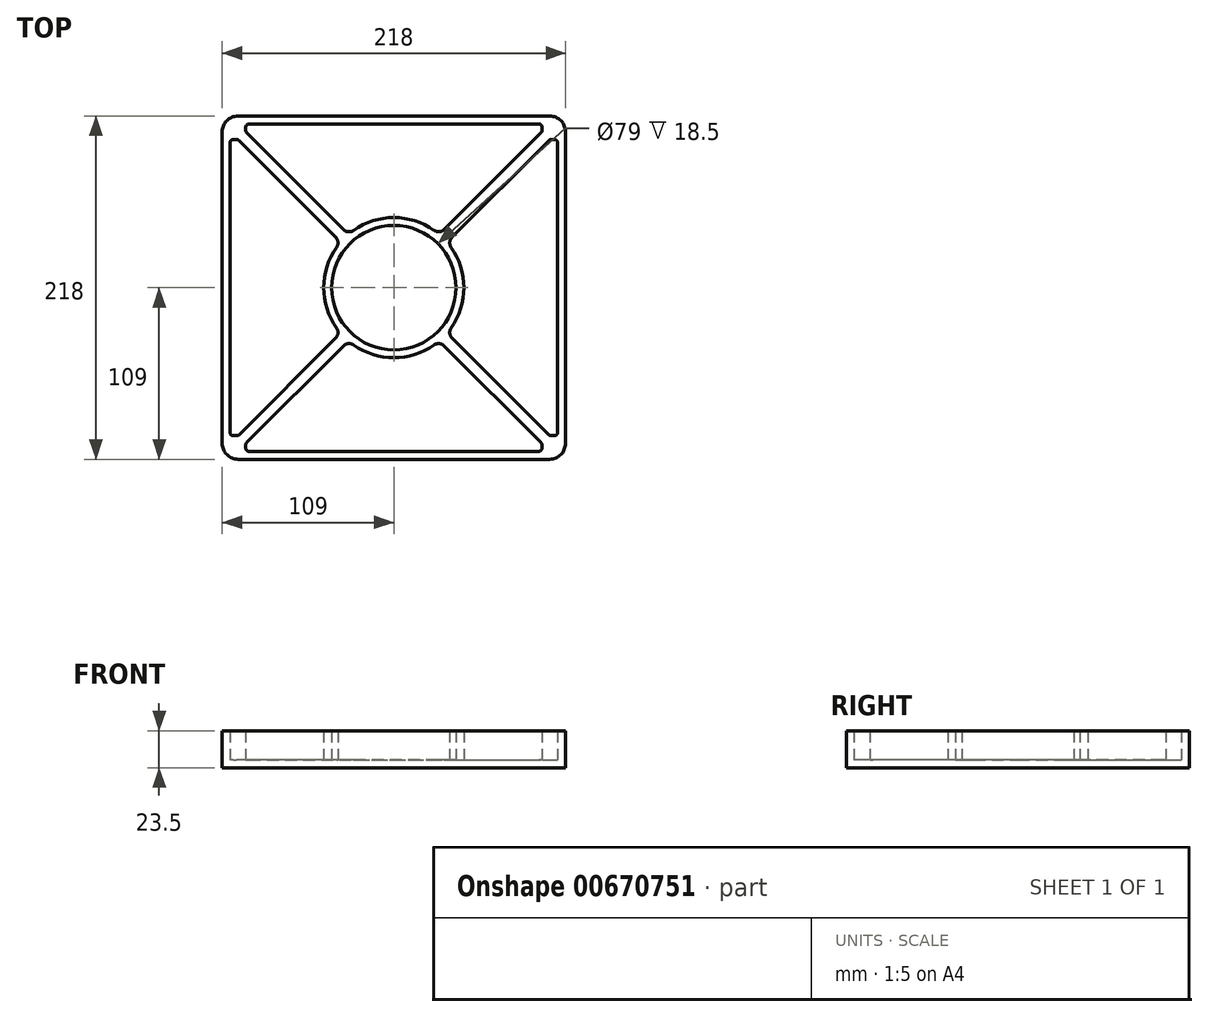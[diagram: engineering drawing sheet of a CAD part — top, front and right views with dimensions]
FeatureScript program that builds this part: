
annotation { "Feature Type Name" : "Feature", "Feature Type Description" : "" }
export const myFeature = defineFeature(function(context is Context, id is Id, definition is map)
    precondition{}
    {
        {
            var Q0;
            Q0=qCreatedBy(makeId("Top.planeOp"),FACE);
            var sketch = newSketch(context, id + "F0", { "sketchPlane" : qUnion([Q0])});
            skLineSegment(sketch, "E0.bottom", {"start": v(-99, 109) * mm, "end": v(99, 109) * mm});
            skLineSegment(sketch, "E0.top", {"start": v(-99, -109) * mm, "end": v(99, -109) * mm});
            skLineSegment(sketch, "E0.left", {"start": v(-109, 99) * mm, "end": v(-109, -99) * mm});
            skLineSegment(sketch, "E0.right", {"start": v(109, 99) * mm, "end": v(109, -99) * mm});
            skLineSegment(sketch, "E1", {"start": v(-109, 109) * mm, "end": v(109, -109) * mm, "construction": true});
            skLineSegment(sketch, "E2", {"start": v(-109, -109) * mm, "end": v(109, 109) * mm, "construction": true});
            skCircle(sketch, "E3", {"center": v(0, 0) * mm, "radius": 39.5 * mm});
            skPoint(sketch, "E4.visualSharp", {"position": v(-109, 109) * mm});
            skArc(sketch, "E4.filletArc", {"start": v(-99, 109) * mm, "mid": v(-106.07, 106.07) * mm, "end": v(-109, 99) * mm});
            skPoint(sketch, "E5.visualSharp", {"position": v(109, 109) * mm});
            skArc(sketch, "E5.filletArc", {"start": v(109, 99) * mm, "mid": v(106.07, 106.07) * mm, "end": v(99, 109) * mm});
            skPoint(sketch, "E6.visualSharp", {"position": v(109, -109) * mm});
            skArc(sketch, "E6.filletArc", {"start": v(99, -109) * mm, "mid": v(106.07, -106.07) * mm, "end": v(109, -99) * mm});
            skPoint(sketch, "E7.visualSharp", {"position": v(-109, -109) * mm});
            skArc(sketch, "E7.filletArc", {"start": v(-109, -99) * mm, "mid": v(-106.07, -106.07) * mm, "end": v(-99, -109) * mm});
            skArc(sketch, "E8.0", {"start": v(-99, 104) * mm, "mid": v(-99.03, 104) * mm, "end": v(-99.05, 104) * mm});
            skLineSegment(sketch, "E8.1", {"start": v(-92.05, 104) * mm, "end": v(-60.86, 104) * mm});
            skLineSegment(sketch, "E8.2", {"start": v(-104, 92.05) * mm, "end": v(-104, 60.86) * mm});
            skArc(sketch, "E8.3", {"start": v(104, 99) * mm, "mid": v(104, 99.03) * mm, "end": v(104, 99.05) * mm});
            skArc(sketch, "E8.4", {"start": v(-104, -99) * mm, "mid": v(-104, -99.03) * mm, "end": v(-104, -99.05) * mm});
            skLineSegment(sketch, "E8.5", {"start": v(-92.05, -104) * mm, "end": v(-60.86, -104) * mm});
            skArc(sketch, "E8.6", {"start": v(99, -104) * mm, "mid": v(99.03, -104) * mm, "end": v(99.05, -104) * mm});
            skLineSegment(sketch, "E8.7", {"start": v(104, 92.05) * mm, "end": v(104, 60.86) * mm});
            skPoint(sketch, "E9.visualSharp", {"position": v(-55.86, 55.86) * mm});
            skPoint(sketch, "E10.visualSharp", {"position": v(55.86, 55.86) * mm});
            skPoint(sketch, "E11.visualSharp", {"position": v(55.86, -55.86) * mm});
            skPoint(sketch, "E12.visualSharp", {"position": v(-55.86, -55.86) * mm});
            skLineSegment(sketch, "E13.trimOffspring", {"start": v(-104, 45.86) * mm, "end": v(-104, -45.86) * mm});
            skLineSegment(sketch, "E14.trimOffspring", {"start": v(-45.86, 104) * mm, "end": v(45.86, 104) * mm});
            skLineSegment(sketch, "E15.trimOffspring", {"start": v(60.86, 104) * mm, "end": v(92.05, 104) * mm});
            skLineSegment(sketch, "E16.trimOffspring", {"start": v(104, 45.86) * mm, "end": v(104, -45.86) * mm});
            skLineSegment(sketch, "E17.trimOffspring", {"start": v(104, -60.86) * mm, "end": v(104, -92.05) * mm});
            skLineSegment(sketch, "E18.trimOffspring", {"start": v(60.86, -104) * mm, "end": v(92.05, -104) * mm});
            skLineSegment(sketch, "E19.trimOffspring", {"start": v(-45.86, -104) * mm, "end": v(45.86, -104) * mm});
            skLineSegment(sketch, "E20.trimOffspring", {"start": v(-104, -60.86) * mm, "end": v(-104, -92.05) * mm});
            skPoint(sketch, "E21.visualSharp", {"position": v(-55.86, 104) * mm});
            skPoint(sketch, "E22.visualSharp", {"position": v(-50.86, 104) * mm});
            skPoint(sketch, "E23.visualSharp", {"position": v(-50.86, 60.45) * mm});
            skPoint(sketch, "E24.visualSharp", {"position": v(-60.45, 50.86) * mm});
            skPoint(sketch, "E25.visualSharp", {"position": v(-104, 50.86) * mm});
            skPoint(sketch, "E26.visualSharp", {"position": v(-104, 55.86) * mm});
            skPoint(sketch, "E27.visualSharp", {"position": v(55.86, 104) * mm});
            skPoint(sketch, "E28.visualSharp", {"position": v(50.86, 104) * mm});
            skPoint(sketch, "E29.visualSharp", {"position": v(50.86, 60.45) * mm});
            skPoint(sketch, "E30.visualSharp", {"position": v(60.45, 50.86) * mm});
            skPoint(sketch, "E31.visualSharp", {"position": v(104, 55.86) * mm});
            skPoint(sketch, "E32.visualSharp", {"position": v(104, 50.86) * mm});
            skPoint(sketch, "E33.visualSharp", {"position": v(104, -50.86) * mm});
            skPoint(sketch, "E34.visualSharp", {"position": v(104, -55.86) * mm});
            skPoint(sketch, "E35.visualSharp", {"position": v(60.45, -50.86) * mm});
            skPoint(sketch, "E36.visualSharp", {"position": v(50.86, -60.45) * mm});
            skPoint(sketch, "E37.visualSharp", {"position": v(55.86, -104) * mm});
            skPoint(sketch, "E38.visualSharp", {"position": v(50.86, -104) * mm});
            skPoint(sketch, "E39.visualSharp", {"position": v(-55.86, -104) * mm});
            skPoint(sketch, "E40.visualSharp", {"position": v(-50.86, -104) * mm});
            skPoint(sketch, "E41.visualSharp", {"position": v(-50.86, -60.45) * mm});
            skPoint(sketch, "E42.visualSharp", {"position": v(-60.45, -50.86) * mm});
            skPoint(sketch, "E43.visualSharp", {"position": v(-104, -50.86) * mm});
            skPoint(sketch, "E44.visualSharp", {"position": v(-104, -55.86) * mm});
            skLineSegment(sketch, "E45", {"start": v(-60.86, 104) * mm, "end": v(-45.86, 104) * mm});
            skLineSegment(sketch, "E46", {"start": v(45.86, 104) * mm, "end": v(60.86, 104) * mm});
            skLineSegment(sketch, "E47", {"start": v(104, 60.86) * mm, "end": v(104, 45.86) * mm});
            skLineSegment(sketch, "E48", {"start": v(104, -45.86) * mm, "end": v(104, -60.86) * mm});
            skLineSegment(sketch, "E49", {"start": v(60.86, -104) * mm, "end": v(45.86, -104) * mm});
            skLineSegment(sketch, "E50", {"start": v(-45.86, -104) * mm, "end": v(-60.86, -104) * mm});
            skLineSegment(sketch, "E51", {"start": v(-104, -60.86) * mm, "end": v(-104, -45.86) * mm});
            skLineSegment(sketch, "E52", {"start": v(-104, 45.86) * mm, "end": v(-104, 60.86) * mm});
            skArc(sketch, "E53.0", {"start": v(-36.4, 25.6) * mm, "mid": v(-44.5, 0) * mm, "end": v(-36.4, -25.6) * mm});
            skLineSegment(sketch, "E54", {"start": v(-36.96, 32) * mm, "end": v(-98.41, 93.46) * mm});
            skLineSegment(sketch, "E55", {"start": v(-32, 36.96) * mm, "end": v(-93.46, 98.41) * mm});
            skLineSegment(sketch, "E56", {"start": v(32, 36.96) * mm, "end": v(93.46, 98.41) * mm});
            skLineSegment(sketch, "E57", {"start": v(36.96, 32) * mm, "end": v(98.41, 93.46) * mm});
            skLineSegment(sketch, "E58", {"start": v(-36.96, -32) * mm, "end": v(-98.41, -93.46) * mm});
            skLineSegment(sketch, "E59", {"start": v(-32, -36.96) * mm, "end": v(-93.46, -98.41) * mm});
            skLineSegment(sketch, "E60", {"start": v(32, -36.96) * mm, "end": v(93.46, -98.41) * mm});
            skLineSegment(sketch, "E61", {"start": v(36.96, -32) * mm, "end": v(98.41, -93.46) * mm});
            skArc(sketch, "E62.trimOffspring", {"start": v(-104, 99.05) * mm, "mid": v(-104, 99.03) * mm, "end": v(-104, 99) * mm});
            skArc(sketch, "E63.trimOffspring", {"start": v(99.05, 104) * mm, "mid": v(99.03, 104) * mm, "end": v(99, 104) * mm});
            skArc(sketch, "E64.trimOffspring", {"start": v(104, -99.05) * mm, "mid": v(104, -99.03) * mm, "end": v(104, -99) * mm});
            skArc(sketch, "E65.trimOffspring", {"start": v(-99.05, -104) * mm, "mid": v(-99.03, -104) * mm, "end": v(-99, -104) * mm});
            skLineSegment(sketch, "E66", {"start": v(-94.05, 99.83) * mm, "end": v(-94.05, 102) * mm});
            skLineSegment(sketch, "E67", {"start": v(-102, 94.05) * mm, "end": v(-99.83, 94.05) * mm});
            skLineSegment(sketch, "E68", {"start": v(94.05, 99.83) * mm, "end": v(94.05, 102) * mm});
            skLineSegment(sketch, "E69", {"start": v(99.83, 94.05) * mm, "end": v(102, 94.05) * mm});
            skLineSegment(sketch, "E70", {"start": v(99.83, -94.05) * mm, "end": v(102, -94.05) * mm});
            skLineSegment(sketch, "E71", {"start": v(94.05, -99.83) * mm, "end": v(94.05, -102) * mm});
            skLineSegment(sketch, "E72", {"start": v(-102, -94.05) * mm, "end": v(-99.83, -94.05) * mm});
            skLineSegment(sketch, "E73", {"start": v(-94.05, -99.83) * mm, "end": v(-94.05, -102) * mm});
            skPoint(sketch, "E74.visualSharp", {"position": v(-94.05, 104) * mm});
            skArc(sketch, "E74.filletArc", {"start": v(-92.05, 104) * mm, "mid": v(-93.46, 103.41) * mm, "end": v(-94.05, 102) * mm});
            skPoint(sketch, "E75.visualSharp", {"position": v(-104, 94.05) * mm});
            skArc(sketch, "E75.filletArc", {"start": v(-102, 94.05) * mm, "mid": v(-103.41, 93.46) * mm, "end": v(-104, 92.05) * mm});
            skPoint(sketch, "E76.visualSharp", {"position": v(-99, 94.05) * mm});
            skArc(sketch, "E76.filletArc", {"start": v(-98.41, 93.46) * mm, "mid": v(-99.06, 93.9) * mm, "end": v(-99.83, 94.05) * mm});
            skPoint(sketch, "E77.visualSharp", {"position": v(-94.05, 99) * mm});
            skArc(sketch, "E77.filletArc", {"start": v(-94.05, 99.83) * mm, "mid": v(-93.9, 99.06) * mm, "end": v(-93.46, 98.41) * mm});
            skPoint(sketch, "E78.visualSharp", {"position": v(94.05, 104) * mm});
            skArc(sketch, "E78.filletArc", {"start": v(94.05, 102) * mm, "mid": v(93.46, 103.41) * mm, "end": v(92.05, 104) * mm});
            skPoint(sketch, "E79.visualSharp", {"position": v(94.05, 99) * mm});
            skArc(sketch, "E79.filletArc", {"start": v(93.46, 98.41) * mm, "mid": v(93.9, 99.06) * mm, "end": v(94.05, 99.83) * mm});
            skPoint(sketch, "E80.visualSharp", {"position": v(99, 94.05) * mm});
            skArc(sketch, "E80.filletArc", {"start": v(99.83, 94.05) * mm, "mid": v(99.06, 93.9) * mm, "end": v(98.41, 93.46) * mm});
            skPoint(sketch, "E81.visualSharp", {"position": v(104, 94.05) * mm});
            skArc(sketch, "E81.filletArc", {"start": v(104, 92.05) * mm, "mid": v(103.41, 93.46) * mm, "end": v(102, 94.05) * mm});
            skPoint(sketch, "E82.visualSharp", {"position": v(104, -94.05) * mm});
            skArc(sketch, "E82.filletArc", {"start": v(102, -94.05) * mm, "mid": v(103.41, -93.46) * mm, "end": v(104, -92.05) * mm});
            skPoint(sketch, "E83.visualSharp", {"position": v(99, -94.05) * mm});
            skArc(sketch, "E83.filletArc", {"start": v(98.41, -93.46) * mm, "mid": v(99.06, -93.9) * mm, "end": v(99.83, -94.05) * mm});
            skPoint(sketch, "E84.visualSharp", {"position": v(94.05, -104) * mm});
            skArc(sketch, "E84.filletArc", {"start": v(92.05, -104) * mm, "mid": v(93.46, -103.41) * mm, "end": v(94.05, -102) * mm});
            skPoint(sketch, "E85.visualSharp", {"position": v(94.05, -99) * mm});
            skArc(sketch, "E85.filletArc", {"start": v(94.05, -99.83) * mm, "mid": v(93.9, -99.06) * mm, "end": v(93.46, -98.41) * mm});
            skPoint(sketch, "E86.visualSharp", {"position": v(-94.05, -104) * mm});
            skArc(sketch, "E86.filletArc", {"start": v(-94.05, -102) * mm, "mid": v(-93.46, -103.41) * mm, "end": v(-92.05, -104) * mm});
            skPoint(sketch, "E87.visualSharp", {"position": v(-94.05, -99) * mm});
            skArc(sketch, "E87.filletArc", {"start": v(-93.46, -98.41) * mm, "mid": v(-93.9, -99.06) * mm, "end": v(-94.05, -99.83) * mm});
            skPoint(sketch, "E88.visualSharp", {"position": v(-104, -94.05) * mm});
            skArc(sketch, "E88.filletArc", {"start": v(-104, -92.05) * mm, "mid": v(-103.41, -93.46) * mm, "end": v(-102, -94.05) * mm});
            skPoint(sketch, "E89.visualSharp", {"position": v(-99, -94.05) * mm});
            skArc(sketch, "E89.filletArc", {"start": v(-99.83, -94.05) * mm, "mid": v(-99.06, -93.9) * mm, "end": v(-98.41, -93.46) * mm});
            skArc(sketch, "E90.trimOffspring", {"start": v(25.6, 36.4) * mm, "mid": v(0, 44.5) * mm, "end": v(-25.6, 36.4) * mm});
            skArc(sketch, "E91.trimOffspring", {"start": v(36.4, -25.6) * mm, "mid": v(44.5, 0) * mm, "end": v(36.4, 25.6) * mm});
            skArc(sketch, "E92.trimOffspring", {"start": v(-25.6, -36.4) * mm, "mid": v(0, -44.5) * mm, "end": v(25.6, -36.4) * mm});
            skPoint(sketch, "E93.visualSharp", {"position": v(-33.84, 28.9) * mm});
            skArc(sketch, "E93.filletArc", {"start": v(-36.4, 25.6) * mm, "mid": v(-35.51, 28.9) * mm, "end": v(-36.96, 32) * mm});
            skPoint(sketch, "E94.visualSharp", {"position": v(-28.9, 33.84) * mm});
            skArc(sketch, "E94.filletArc", {"start": v(-32, 36.96) * mm, "mid": v(-28.9, 35.51) * mm, "end": v(-25.6, 36.4) * mm});
            skPoint(sketch, "E95.visualSharp", {"position": v(28.9, 33.84) * mm});
            skArc(sketch, "E95.filletArc", {"start": v(25.6, 36.4) * mm, "mid": v(28.9, 35.51) * mm, "end": v(32, 36.96) * mm});
            skPoint(sketch, "E96.visualSharp", {"position": v(33.84, 28.9) * mm});
            skArc(sketch, "E96.filletArc", {"start": v(36.96, 32) * mm, "mid": v(35.51, 28.9) * mm, "end": v(36.4, 25.6) * mm});
            skPoint(sketch, "E97.visualSharp", {"position": v(33.84, -28.9) * mm});
            skArc(sketch, "E97.filletArc", {"start": v(36.4, -25.6) * mm, "mid": v(35.51, -28.9) * mm, "end": v(36.96, -32) * mm});
            skPoint(sketch, "E98.visualSharp", {"position": v(28.9, -33.84) * mm});
            skArc(sketch, "E98.filletArc", {"start": v(32, -36.96) * mm, "mid": v(28.9, -35.51) * mm, "end": v(25.6, -36.4) * mm});
            skPoint(sketch, "E99.visualSharp", {"position": v(-28.9, -33.84) * mm});
            skArc(sketch, "E99.filletArc", {"start": v(-25.6, -36.4) * mm, "mid": v(-28.9, -35.51) * mm, "end": v(-32, -36.96) * mm});
            skPoint(sketch, "E100.visualSharp", {"position": v(-33.84, -28.9) * mm});
            skArc(sketch, "E100.filletArc", {"start": v(-36.96, -32) * mm, "mid": v(-35.51, -28.9) * mm, "end": v(-36.4, -25.6) * mm});
            skSolve(sketch);
        }
        {
            var Q0;
            Q0=makeQuery(id+"F0.imprint","IMPRINT",FACE,{"disambiguationData":[TD([[makeQuery(id+"F0.imprint","IMPRINT",EDGE,{"derivedFrom":sQuery(id+"F0.wireOp",EDGE,"E0.bottom")}),-1.0]])]});
            var Q1;
            Q1=makeQuery(id+"F0.imprint","IMPRINT",FACE,{"disambiguationData":[TD([[makeQuery(id+"F0.imprint","IMPRINT",EDGE,{"derivedFrom":sQuery(id+"F0.wireOp",EDGE,"E8.2")}),1.0]])]});
            var Q2;
            Q2=makeQuery(id+"F0.imprint","IMPRINT",FACE,{"disambiguationData":[TD([[makeQuery(id+"F0.imprint","IMPRINT",EDGE,{"derivedFrom":sQuery(id+"F0.wireOp",EDGE,"E8.1")}),-1.0]])]});
            var Q3;
            Q3=makeQuery(id+"F0.imprint","IMPRINT",FACE,{"disambiguationData":[TD([[makeQuery(id+"F0.imprint","IMPRINT",EDGE,{"derivedFrom":sQuery(id+"F0.wireOp",EDGE,"E3")}),1.0]])]});
            var Q4;
            Q4=makeQuery(id+"F0.imprint","IMPRINT",FACE,{"disambiguationData":[TD([[makeQuery(id+"F0.imprint","IMPRINT",EDGE,{"derivedFrom":sQuery(id+"F0.wireOp",EDGE,"E8.7")}),-1.0]])]});
            var Q5;
            Q5=makeQuery(id+"F0.imprint","IMPRINT",FACE,{"disambiguationData":[TD([[makeQuery(id+"F0.imprint","IMPRINT",EDGE,{"derivedFrom":sQuery(id+"F0.wireOp",EDGE,"E8.5")}),1.0]])]});
            extrude(context, id + "F1", {"entities" : qUnion([Q0, Q1, Q2, Q3, Q4, Q5]), "oppositeDirection" : true, "depth" : 5 * mm, "offsetDistance" : 25 * mm});
        }
        {
            var Q0;
            Q0 = qSketchRegion(id + "F0", true);
            extrude(context, id + "F2", {"entities" : qUnion([Q0]), "operationType" : NewBodyOperationType.ADD, "depth" : 18.5 * mm, "offsetDistance" : 25 * mm});
        }
    });
